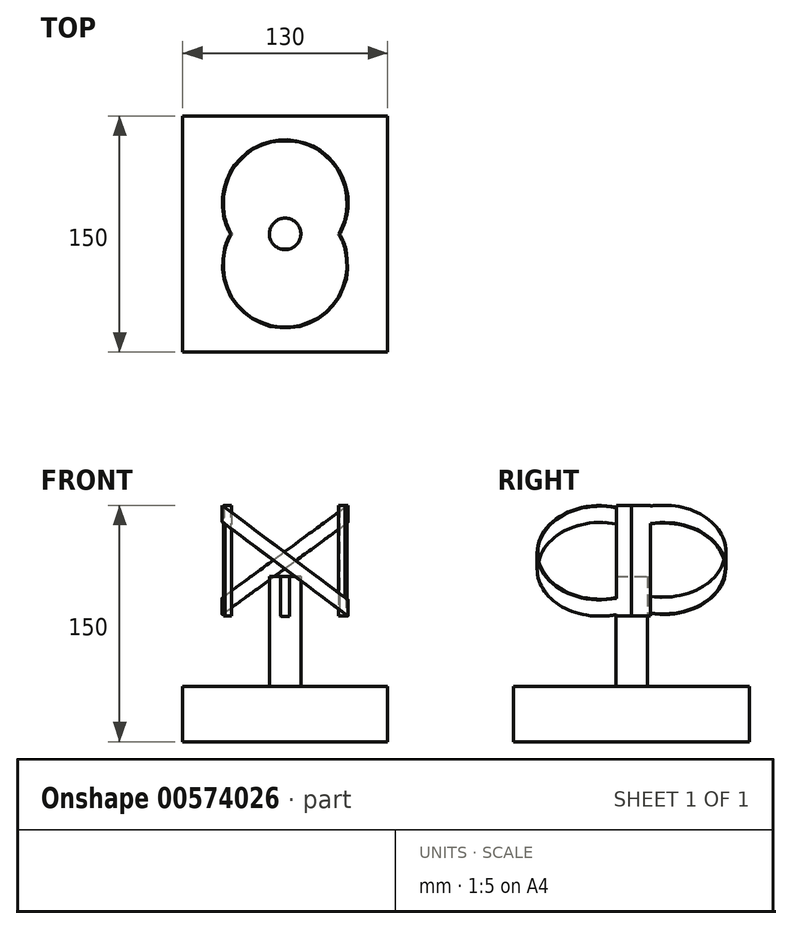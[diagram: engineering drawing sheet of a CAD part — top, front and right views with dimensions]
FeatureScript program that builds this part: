
annotation { "Feature Type Name" : "Feature", "Feature Type Description" : "" }
export const myFeature = defineFeature(function(context is Context, id is Id, definition is map)
    precondition{}
    {
        {
            var Q0;
            Q0=qCreatedBy(makeId("Top.planeOp"),FACE);
            var sketch = newSketch(context, id + "F0", { "sketchPlane" : qUnion([Q0])});
            skLineSegment(sketch, "E0", {"start": v(-147.94, 0) * mm, "end": v(-147.94, 75) * mm});
            skLineSegment(sketch, "E1", {"start": v(-147.94, 75) * mm, "end": v(-17.94, 75) * mm});
            skLineSegment(sketch, "E2", {"start": v(-17.94, 75) * mm, "end": v(-17.94, 0) * mm});
            skLineSegment(sketch, "E3", {"start": v(-17.94, 0) * mm, "end": v(-147.94, 0) * mm, "construction": true});
            skLineSegment(sketch, "E4.MirrorCS", {"start": v(-147.94, 0) * mm, "end": v(-147.94, -75) * mm});
            skLineSegment(sketch, "E5.MirrorCS", {"start": v(-147.94, -75) * mm, "end": v(-17.94, -75) * mm});
            skLineSegment(sketch, "E6.MirrorCS", {"start": v(-17.94, -75) * mm, "end": v(-17.94, 0) * mm});
            skSolve(sketch);
        }
        {
            var Q0;
            Q0 = qSketchRegion(id + "F0", true);
            var Q1;
            Q1=makeQuery(id+"F0.imprint","IMPRINT",FACE,{"disambiguationData":[TD([[makeQuery(id+"F0.imprint","IMPRINT",EDGE,{"derivedFrom":sQuery(id+"F0.wireOp",EDGE,"E0")}),-1.0]])]});
            extrude(context, id + "F1", {"entities" : qUnion([Q0, Q1]), "depth" : 35 * mm, "offsetDistance" : 25 * mm});
        }
        {
            var Q0;
            Q0=makeQuery(id+"F1.opExtrude","CAP_FACE",FACE,{"disambiguationData":[OSD([sQuery(id+"F0.wireOp",EDGE,"E0"),sQuery(id+"F0.wireOp",EDGE,"E1"),sQuery(id+"F0.wireOp",EDGE,"E2"),sQuery(id+"F0.wireOp",EDGE,"E4.MirrorCS"),sQuery(id+"F0.wireOp",EDGE,"E5.MirrorCS"),sQuery(id+"F0.wireOp",EDGE,"E6.MirrorCS")])],"isStart":false});
            var sketch = newSketch(context, id + "F2", { "sketchPlane" : qUnion([Q0])});
            skCircle(sketch, "E7", {"center": v(-82.94, 0) * mm, "radius": 10 * mm});
            skPoint(sketch, "E7.centerSnap0", {"position": v(-82.94, 75) * mm});
            skSolve(sketch);
        }
        {
            var Q0;
            Q0 = qSketchRegion(id + "F2", true);
            extrude(context, id + "F3", {"entities" : qUnion([Q0]), "operationType" : NewBodyOperationType.ADD, "depth" : 45 * mm, "offsetDistance" : 25 * mm});
        }
        {
            var Q0;
            Q0=makeQuery(id+"F3.opExtrude","CAP_FACE",FACE,{"disambiguationData":[OSD([sQuery(id+"F2.wireOp",EDGE,"E7")])],"isStart":false});
            var sketch = newSketch(context, id + "F4", { "sketchPlane" : qUnion([Q0])});
            skLineSegment(sketch, "E8", {"start": v(-82.94, 0) * mm, "end": v(-82.94, 20) * mm});
            skLineSegment(sketch, "E9", {"start": v(-82.94, 0) * mm, "end": v(-82.94, -20) * mm, "construction": true});
            skCircle(sketch, "E10", {"center": v(-82.94, -20) * mm, "radius": 40 * mm});
            skCircle(sketch, "E11", {"center": v(-82.94, 20) * mm, "radius": 40 * mm});
            skCircle(sketch, "E12", {"center": v(-82.94, 20) * mm, "radius": 39.5 * mm});
            skCircle(sketch, "E13", {"center": v(-82.94, -20) * mm, "radius": 39.5 * mm});
            skSolve(sketch);
        }
        {
            var Q0;
            Q0 = qSketchRegion(id + "F4", true);
            var Q1;
            Q1 = qSketchRegion(id + "F2", true);
            extrude(context, id + "F5", {"entities" : qUnion([Q0, Q1]), "operationType" : NewBodyOperationType.ADD, "depth" : 70 * mm, "offsetDistance" : 25 * mm});
        }
        {
            var Q0;
            Q0=makeQuery(id+"F1.opExtrude","SWEPT_FACE",FACE,{"disambiguationData":[OSD([sQuery(id+"F0.wireOp",EDGE,"E1")])]});
            var sketch = newSketch(context, id + "F6", { "sketchPlane" : qUnion([Q0])});
            skLineSegment(sketch, "E14", {"start": v(42.92, 150.28) * mm, "end": v(123.42, 91.01) * mm});
            skLineSegment(sketch, "E15", {"start": v(123.42, 91.01) * mm, "end": v(145.3, 160.42) * mm});
            skLineSegment(sketch, "E16", {"start": v(145.3, 160.42) * mm, "end": v(39.75, 157.89) * mm});
            skLineSegment(sketch, "E17", {"start": v(39.75, 157.89) * mm, "end": v(42.92, 150.28) * mm});
            skLineSegment(sketch, "E18", {"start": v(42.6, 139.5) * mm, "end": v(125.32, 78.97) * mm});
            skLineSegment(sketch, "E19", {"start": v(125.32, 78.97) * mm, "end": v(115.5, 72.63) * mm});
            skLineSegment(sketch, "E20", {"start": v(115.5, 72.63) * mm, "end": v(96.8, 78.97) * mm});
            skLineSegment(sketch, "E21", {"start": v(96.8, 78.97) * mm, "end": v(35.63, 78.97) * mm});
            skLineSegment(sketch, "E22", {"start": v(35.63, 78.97) * mm, "end": v(42.6, 139.5) * mm});
            skSolve(sketch);
        }
        {
            var Q0;
            Q0 = qSketchRegion(id + "F6", true);
            extrude(context, id + "F7", {"entities" : qUnion([Q0]), "operationType" : NewBodyOperationType.REMOVE, "oppositeDirection" : true, "depth" : 63 * mm, "offsetDistance" : 25 * mm});
        }
        {
            var Q0;
            Q0=makeQuery(id+"F1.opExtrude","SWEPT_FACE",FACE,{"disambiguationData":[OSD([sQuery(id+"F0.wireOp",EDGE,"E5.MirrorCS")])]});
            var sketch = newSketch(context, id + "F8", { "sketchPlane" : qUnion([Q0])});
            skLineSegment(sketch, "E23", {"start": v(-123.14, 150.14) * mm, "end": v(-42.6, 89.78) * mm});
            skLineSegment(sketch, "E24", {"start": v(-42.6, 89.78) * mm, "end": v(-33.78, 154.05) * mm});
            skLineSegment(sketch, "E25", {"start": v(-33.78, 154.05) * mm, "end": v(-123.14, 150.14) * mm});
            skLineSegment(sketch, "E26", {"start": v(-42.6, 79.4) * mm, "end": v(-126.34, 142.15) * mm});
            skLineSegment(sketch, "E27", {"start": v(-126.34, 142.15) * mm, "end": v(-126.34, 79.98) * mm});
            skLineSegment(sketch, "E28", {"start": v(-126.34, 79.98) * mm, "end": v(-42.6, 79.4) * mm});
            skSolve(sketch);
        }
        {
            var Q0;
            Q0 = qSketchRegion(id + "F8", true);
            extrude(context, id + "F9", {"entities" : qUnion([Q0]), "operationType" : NewBodyOperationType.REMOVE, "oppositeDirection" : true, "depth" : 65.4 * mm, "offsetDistance" : 25 * mm});
        }
    });
